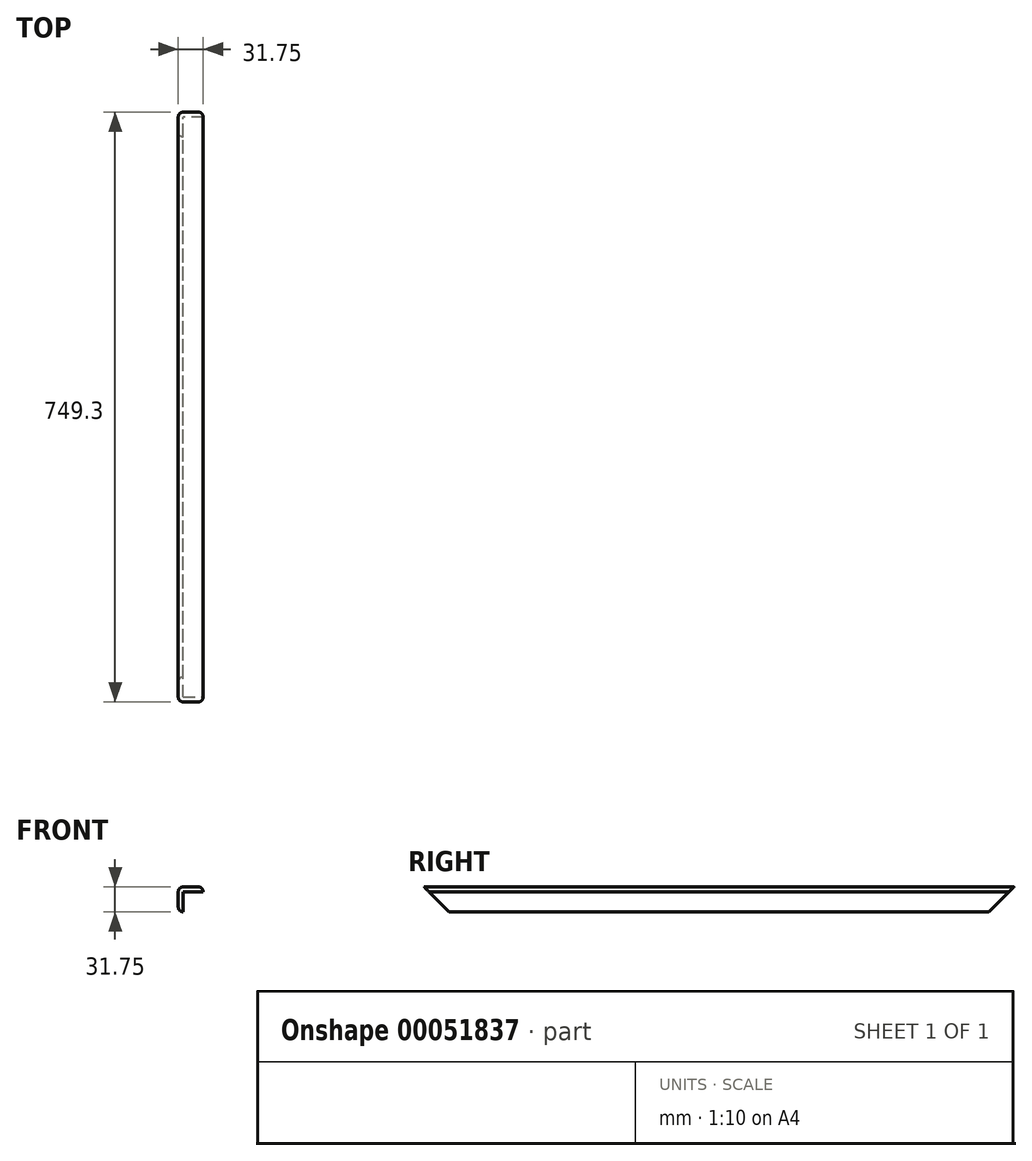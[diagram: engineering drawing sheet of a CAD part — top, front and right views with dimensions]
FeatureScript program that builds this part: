
annotation { "Feature Type Name" : "Feature", "Feature Type Description" : "" }
export const myFeature = defineFeature(function(context is Context, id is Id, definition is map)
    precondition{}
    {
        {
            var Q0;
            Q0=qCreatedBy(makeId("Front.planeOp"),FACE);
            var sketch = newSketch(context, id + "F0", { "sketchPlane" : qUnion([Q0])});
            skLineSegment(sketch, "E0", {"start": v(0, 0) * mm, "end": v(0, -25.4) * mm});
            skLineSegment(sketch, "E1", {"start": v(0, 0) * mm, "end": v(25.4, 0) * mm});
            skLineSegment(sketch, "E2.0", {"start": v(-6.35, 0) * mm, "end": v(-6.35, -19.05) * mm});
            skLineSegment(sketch, "E3.0", {"start": v(0, 6.35) * mm, "end": v(19.05, 6.35) * mm});
            skLineSegment(sketch, "E4", {"start": v(25.4, 0) * mm, "end": v(25.4, 0) * mm});
            skLineSegment(sketch, "E5", {"start": v(0, -25.4) * mm, "end": v(0, -25.4) * mm});
            skPoint(sketch, "E6.visualSharp", {"position": v(-6.35, -25.4) * mm});
            skArc(sketch, "E6.filletArc", {"start": v(-6.35, -19.05) * mm, "mid": v(-4.5, -23.54) * mm, "end": v(0, -25.4) * mm});
            skPoint(sketch, "E7.visualSharp", {"position": v(-6.35, 6.35) * mm});
            skArc(sketch, "E7.filletArc", {"start": v(0, 6.35) * mm, "mid": v(-4.5, 4.5) * mm, "end": v(-6.35, 0) * mm});
            skPoint(sketch, "E8.visualSharp", {"position": v(25.4, 6.35) * mm});
            skArc(sketch, "E8.filletArc", {"start": v(25.4, 0) * mm, "mid": v(23.54, 4.5) * mm, "end": v(19.05, 6.35) * mm});
            skSolve(sketch);
        }
        {
            var Q0;
            Q0=makeQuery(id+"F0.imprint","IMPRINT",FACE,{"disambiguationData":[TD([[makeQuery(id+"F0.imprint","IMPRINT",EDGE,{"derivedFrom":sQuery(id+"F0.wireOp",EDGE,"E0")}),-1.0]])]});
            extrude(context, id + "F1", {"entities" : qUnion([Q0]), "depth" : 749.3 * mm});
        }
        {
            var Q0;
            Q0=makeQuery(id+"F1.opExtrude","SWEPT_FACE",FACE,{"disambiguationData":[OSD([sQuery(id+"F0.wireOp",EDGE,"E2.0")])]});
            var sketch = newSketch(context, id + "F2", { "sketchPlane" : qUnion([Q0])});
            skLineSegment(sketch, "E9", {"start": v(749.3, 6.35) * mm, "end": v(717.55, -25.4) * mm});
            skLineSegment(sketch, "E10", {"start": v(717.55, -25.4) * mm, "end": v(749.3, -25.4) * mm});
            skLineSegment(sketch, "E11", {"start": v(749.3, -25.4) * mm, "end": v(749.3, 6.35) * mm});
            skSolve(sketch);
        }
        {
            var Q0;
            Q0=qSketchRegion(id+"F2",true);
            extrude(context, id + "F3", {"entities" : qUnion([Q0]), "operationType" : NewBodyOperationType.REMOVE, "endBound" : BoundingType.UP_TO_NEXT, "oppositeDirection" : true, "depth" : 25.4 * mm});
        }
        {
            var Q0;
            Q0=makeQuery(id+"F1.opExtrude","SWEPT_FACE",FACE,{"disambiguationData":[OSD([sQuery(id+"F0.wireOp",EDGE,"E2.0")])]});
            var sketch = newSketch(context, id + "F4", { "sketchPlane" : qUnion([Q0])});
            skLineSegment(sketch, "E12", {"start": v(0, 6.35) * mm, "end": v(31.75, -25.4) * mm});
            skLineSegment(sketch, "E13", {"start": v(31.75, -25.4) * mm, "end": v(0, -25.4) * mm});
            skLineSegment(sketch, "E14", {"start": v(0, -25.4) * mm, "end": v(0, 6.35) * mm});
            skSolve(sketch);
        }
        {
            var Q0;
            {var subQ0=sQuery(id+"F4.wireOp",EDGE,"E13");Q0=makeQuery(id+"F4.imprint","IMPRINT",FACE,{"disambiguationData":[TD([[makeQuery(id+"F4.imprint","IMPRINT",EDGE,{"derivedFrom":subQ0}),-1.0]])]});}
            var Q1;
            {var subQ0=sQuery(id+"F4.wireOp",EDGE,"E12");var subQ1=sQuery(id+"F0.wireOp",EDGE,"E2.0");var subQ2=makeQuery(id+"F1.opExtrude","SWEPT_EDGE",EDGE,{"disambiguationData":[OSD([subQ1,sQuery(id+"F0.wireOp",EDGE,"E7.filletArc")])]});var subQ3=makeQuery(id+"F4.imprint","INTERSECT",VERTEX,{"derivedFrom":[subQ2,subQ0]});Q1=makeQuery(id+"F4.imprint","IMPRINT",FACE,{"disambiguationData":[TD([[makeQuery(id+"F4.imprint","IMPRINT",EDGE,{"disambiguationData":[TD([[subQ3,-1.0]])],"derivedFrom":subQ0}),-1.0]])]});}
            var Q2;
            {var subQ0=sQuery(id+"F4.wireOp",EDGE,"E14");var subQ1=sQuery(id+"F4.wireOp",EDGE,"E12");var subQ2=makeQuery(id+"F4.imprint","INTERSECT",VERTEX,{"derivedFrom":[subQ1,subQ0]});Q2=makeQuery(id+"F4.imprint","IMPRINT",FACE,{"disambiguationData":[TD([[makeQuery(id+"F4.imprint","IMPRINT",EDGE,{"disambiguationData":[TD([[subQ2,-1.0]])],"derivedFrom":subQ1}),-1.0]])]});}
            extrude(context, id + "F5", {"entities" : qUnion([Q0, Q1, Q2]), "operationType" : NewBodyOperationType.REMOVE, "oppositeDirection" : true, "depth" : 50.8 * mm});
        }
    });
